# Revit family: TopVent_TH
name_source: partatom
category: Mechanical Equipment
revit_build: Autodesk Revit MEP 2015 (Build: 20160512_0715(x64)
units: mm (PartAtom-declared; Revit-internal decimal feet)

## types (6) — shared parameters
COBIE Extract air temperature max. = 50°C
COBIE Frequency = 50 Hz
COBIE Permitted voltage tolerance = +/-5%
COBIE Pressure of the heating medium max. = 800 kPa
COBIE Protection rating = IP 54
COBIE Series fuse = 13A
COBIE Supply air temperature max. = 60°C
COBIE Supply voltage = 3x400 V AC
COBIE Temperature of the heating medium max. = 90°C
Extract air temperature max. = 50°C
Frequency = 50 Hz
Permitted voltage tolerance = +/-5%
Pressure of the heating medium max. = 800 kPa
Protection rating = IP 54
Series fuse = 13A
Supply air temperature max. = 60°C
Supply voltage = 3x400 V AC
Temperature of the heating medium max. = 90°C

## per-type parameters (varying)
- TH-6-A: A=900 mm  [stored 2.95276 ft]; B=905 mm  [stored 2.96916 ft]; C=415 mm  [stored 1.36155 ft]; COBIE Connected load=1.5 kW; COBIE Current consumption max.=2.9A; COBIE Effective electric power input=0.46 kW; COBIE Floor area covered=537.0; COBIE Heat output 16/20 °C (60/40 °C)=18.8/16.2 kW; COBIE Heat output 16/20 °C (80/60 °C)=32.8/30.3 kW; COBIE Maximum mounting height 16/20 °C (60/40 °C)=16.8/17.9 m; COBIE Maximum mounting height 16/20 °C (80/60 °C)=13.4/14.0 m; COBIE Nominal air flow rate=6000.0; COBIE Octave sound power level - 1000 Hz=74 dB; COBIE Octave sound power level - 125 Hz=60 dB; COBIE Octave sound power level - 2000 Hz=70 dB; COBIE Octave sound power level - 250 Hz=65 dB; COBIE Octave sound power level - 4000 Hz=64 dB; COBIE Octave sound power level - 500 Hz=70 dB; COBIE Octave sound power level - 63 Hz=55 dB; COBIE Octave sound power level - 8000 Hz=56 dB; COBIE Sound pressure level (at a distance of 5 m)=55 dB(A); COBIE Static efficiency of the fans=48.5%; COBIE Supply air temperature 16/20 °C (60/40 °C)=27.3/30.0 °C; COBIE Supply air temperature 16/20 °C (80/60 °C)=34.2/37.0 °C; COBIE Total sound power level=77 dB(A); COBIE Water content of heating coil=4.6 l; COBIE Water pressure drop 16/20 °C (60/40 °C)=2/2 kPa; COBIE Water pressure drop 16/20 °C (80/60 °C)=7/6 kPa; COBIE Water quantity 16/20 °C (60/40 °C)=807/697 l/h; COBIE Water quantity 16/20 °C (80/60 °C)=1410/1301 l/h; COBIE Weight=104 kg; Connected load=1.5 kW; Current consumption max.=2.9A; E=594 mm  [stored 1.94882 ft]; E/2=297 mm  [stored 0.974409 ft]; Effective electric power input=0.46 kW; F=758 mm  [stored 2.48688 ft]; Floor area covered=537 m²; G=322 mm  [stored 1.05643 ft]; H=244 mm  [stored 0.800525 ft]; Heat output 16/20 °C (60/40 °C)=18.8/16.2 kW; Heat output 16/20 °C (80/60 °C)=32.8/30.3 kW; I=760 mm  [stored 2.49344 ft]; J=32 mm; K=1030 mm  [stored 3.37927 ft]; Maximum mounting height 16/20 °C (60/40 °C)=16.8/17.9 m; Maximum mounting height 16/20 °C (80/60 °C)=13.4/14.0 m; Nominal air flow rate=6000 m³/h; Octave sound power level - 1000 Hz=74 dB; Octave sound power level - 125 Hz=60 dB; Octave sound power level - 2000 Hz=70 dB; Octave sound power level - 250 Hz=65 dB; Octave sound power level - 4000 Hz=64 dB; Octave sound power level - 500 Hz=70 dB; Octave sound power level - 63 Hz=55 dB; Octave sound power level - 8000 Hz=56 dB; R=977 mm  [stored 3.20538 ft]; Sound pressure level (at a distance of 5 m)=55 dB(A); Static efficiency of the fans=48.5%; Supply air temperature 16/20 °C (60/40 °C)=27.3/30.0 °C; Supply air temperature 16/20 °C (80/60 °C)=34.2/37.0 °C; Total sound power level=77 dB(A); Water content of heating coil=4.6 l; Water pressure drop 16/20 °C (60/40 °C)=2/2 kPa; Water pressure drop 16/20 °C (80/60 °C)=7/6 kPa; Water quantity 16/20 °C (60/40 °C)=807/697 l/h; Water quantity 16/20 °C (80/60 °C)=1410/1301 l/h; Weight=104 kg
- TH-6-B: A=900 mm  [stored 2.95276 ft]; B=905 mm  [stored 2.96916 ft]; C=415 mm  [stored 1.36155 ft]; COBIE Connected load=1.5 kW; COBIE Current consumption max.=2.9A; COBIE Effective electric power input=0.53 kW; COBIE Floor area covered=537.0; COBIE Heat output 16/20 °C (60/40 °C)=26.9/23.3 kW; COBIE Heat output 16/20 °C (80/60 °C)=47.0/43.4 kW; COBIE Maximum mounting height 16/20 °C (60/40 °C)=14.6/15.5 m; COBIE Maximum mounting height 16/20 °C (80/60 °C)=11.6/12.0 m; COBIE Nominal air flow rate=6000.0; COBIE Octave sound power level - 1000 Hz=74 dB; COBIE Octave sound power level - 125 Hz=60 dB; COBIE Octave sound power level - 2000 Hz=70 dB; COBIE Octave sound power level - 250 Hz=65 dB; COBIE Octave sound power level - 4000 Hz=64 dB; COBIE Octave sound power level - 500 Hz=70 dB; COBIE Octave sound power level - 63 Hz=55 dB; COBIE Octave sound power level - 8000 Hz=56 dB; COBIE Sound pressure level (at a distance of 5 m)=55 dB(A); COBIE Static efficiency of the fans=48.5%; COBIE Supply air temperature 16/20 °C (60/40 °C)=31.1/33.5 °C; COBIE Supply air temperature 16/20 °C (80/60 °C)=41.3/43.5 °C; COBIE Total sound power level=77 dB(A); COBIE Water content of heating coil=4.6 l; COBIE Water pressure drop 16/20 °C (60/40 °C)=4/3 kPa; COBIE Water pressure drop 16/20 °C (80/60 °C)=13/11 kPa; COBIE Water quantity 16/20 °C (60/40 °C)=1157/1001 l/h; COBIE Water quantity 16/20 °C (80/60 °C)=2020/1864 l/h; COBIE Weight=104 kg; Connected load=1.5 kW; Current consumption max.=2.9A; E=594 mm  [stored 1.94882 ft]; E/2=297 mm  [stored 0.974409 ft]; Effective electric power input=0.53 kW; F=758 mm  [stored 2.48688 ft]; Floor area covered=537 m²; G=322 mm  [stored 1.05643 ft]; H=244 mm  [stored 0.800525 ft]; Heat output 16/20 °C (60/40 °C)=26.9/23.3 kW; Heat output 16/20 °C (80/60 °C)=47.0/43.4 kW; I=760 mm  [stored 2.49344 ft]; J=32 mm; K=1030 mm  [stored 3.37927 ft]; Maximum mounting height 16/20 °C (60/40 °C)=14.6/15.5 m; Maximum mounting height 16/20 °C (80/60 °C)=11.6/12.0 m; Nominal air flow rate=6000 m³/h; Octave sound power level - 1000 Hz=74 dB; Octave sound power level - 125 Hz=60 dB; Octave sound power level - 2000 Hz=70 dB; Octave sound power level - 250 Hz=65 dB; Octave sound power level - 4000 Hz=64 dB; Octave sound power level - 500 Hz=70 dB; Octave sound power level - 63 Hz=55 dB; Octave sound power level - 8000 Hz=56 dB; R=977 mm  [stored 3.20538 ft]; Sound pressure level (at a distance of 5 m)=55 dB(A); Static efficiency of the fans=48.5%; Supply air temperature 16/20 °C (60/40 °C)=31.1/33.5 °C; Supply air temperature 16/20 °C (80/60 °C)=41.3/43.5 °C; Total sound power level=77 dB(A); Water content of heating coil=4.6 l; Water pressure drop 16/20 °C (60/40 °C)=4/3 kPa; Water pressure drop 16/20 °C (80/60 °C)=13/11 kPa; Water quantity 16/20 °C (60/40 °C)=1157/1001 l/h; Water quantity 16/20 °C (80/60 °C)=2020/1864 l/h; Weight=104 kg
- TH-6-C: A=900 mm  [stored 2.95276 ft]; B=905 mm  [stored 2.96916 ft]; C=415 mm  [stored 1.36155 ft]; COBIE Connected load=1.5 kW; COBIE Current consumption max.=2.9A; COBIE Effective electric power input=0.74 kW; COBIE Floor area covered=537.0; COBIE Heat output 16/20 °C (60/40 °C)=45.0/39.3 kW; COBIE Heat output 16/20 °C (80/60 °C)=76.0/70.3 kW; COBIE Maximum mounting height 16/20 °C (60/40 °C)=11.8/12.5 m; COBIE Maximum mounting height 16/20 °C (80/60 °C)=9.4/9.8 m; COBIE Nominal air flow rate=6000.0; COBIE Octave sound power level - 1000 Hz=74 dB; COBIE Octave sound power level - 125 Hz=60 dB; COBIE Octave sound power level - 2000 Hz=70 dB; COBIE Octave sound power level - 250 Hz=65 dB; COBIE Octave sound power level - 4000 Hz=64 dB; COBIE Octave sound power level - 500 Hz=70 dB; COBIE Octave sound power level - 63 Hz=55 dB; COBIE Octave sound power level - 8000 Hz=56 dB; COBIE Sound pressure level (at a distance of 5 m)=55 dB(A); COBIE Static efficiency of the fans=48.5%; COBIE Supply air temperature 16/20 °C (60/40 °C)=40.3/41.5 °C; COBIE Supply air temperature 16/20 °C (80/60 °C)=55.6/56.8 °C; COBIE Total sound power level=77 dB(A); COBIE Water content of heating coil=7.9 l; COBIE Water pressure drop 16/20 °C (60/40 °C)=6/5 kPa; COBIE Water pressure drop 16/20 °C (80/60 °C)=18/16 kPa; COBIE Water quantity 16/20 °C (60/40 °C)=1935/1690 l/h; COBIE Water quantity 16/20 °C (80/60 °C)=3267/3022 l/h; COBIE Weight=111 kg; Connected load=1.5 kW; Current consumption max.=2.9A; E=594 mm  [stored 1.94882 ft]; E/2=297 mm  [stored 0.974409 ft]; Effective electric power input=0.74 kW; F=758 mm  [stored 2.48688 ft]; Floor area covered=537 m²; G=322 mm  [stored 1.05643 ft]; H=244 mm  [stored 0.800525 ft]; Heat output 16/20 °C (60/40 °C)=45.0/39.3 kW; Heat output 16/20 °C (80/60 °C)=76.0/70.3 kW; I=760 mm  [stored 2.49344 ft]; J=32 mm; K=1030 mm  [stored 3.37927 ft]; Maximum mounting height 16/20 °C (60/40 °C)=11.8/12.5 m; Maximum mounting height 16/20 °C (80/60 °C)=9.4/9.8 m; Nominal air flow rate=6000 m³/h; Octave sound power level - 1000 Hz=74 dB; Octave sound power level - 125 Hz=60 dB; Octave sound power level - 2000 Hz=70 dB; Octave sound power level - 250 Hz=65 dB; Octave sound power level - 4000 Hz=64 dB; Octave sound power level - 500 Hz=70 dB; Octave sound power level - 63 Hz=55 dB; Octave sound power level - 8000 Hz=56 dB; R=977 mm  [stored 3.20538 ft]; Sound pressure level (at a distance of 5 m)=55 dB(A); Static efficiency of the fans=48.5%; Supply air temperature 16/20 °C (60/40 °C)=40.3/41.5 °C; Supply air temperature 16/20 °C (80/60 °C)=55.6/56.8 °C; Total sound power level=77 dB(A); Water content of heating coil=7.9 l; Water pressure drop 16/20 °C (60/40 °C)=6/5 kPa; Water pressure drop 16/20 °C (80/60 °C)=18/16 kPa; Water quantity 16/20 °C (60/40 °C)=1935/1690 l/h; Water quantity 16/20 °C (80/60 °C)=3267/3022 l/h; Weight=111 kg
- TH-9-A: A=1100 mm; B=1050 mm; C=480 mm  [stored 1.5748 ft]; COBIE Connected load=2.1 kW; COBIE Current consumption max.=4.0A; COBIE Effective electric power input=0.84 kW; COBIE Floor area covered=946.0; COBIE Heat output 16/20 °C (60/40 °C)=31.7/27.4 kW; COBIE Heat output 16/20 °C (80/60 °C)=55.5/51.2 kW; COBIE Maximum mounting height 16/20 °C (60/40 °C)=17.0/18.1 m; COBIE Maximum mounting height 16/20 °C (80/60 °C)=13.6/14.1 m; COBIE Nominal air flow rate=9000.0; COBIE Octave sound power level - 1000 Hz=75 dB; COBIE Octave sound power level - 125 Hz=65 dB; COBIE Octave sound power level - 2000 Hz=75 dB; COBIE Octave sound power level - 250 Hz=69 dB; COBIE Octave sound power level - 4000 Hz=70 dB; COBIE Octave sound power level - 500 Hz=73 dB; COBIE Octave sound power level - 63 Hz=61 dB; COBIE Octave sound power level - 8000 Hz=63 dB; COBIE Sound pressure level (at a distance of 5 m)=58 dB(A); COBIE Static efficiency of the fans=43.0%; COBIE Supply air temperature 16/20 °C (60/40 °C)=28.5/31.1 °C; COBIE Supply air temperature 16/20 °C (80/60 °C)=36.6/38.9 °C; COBIE Total sound power level=80 dB(A); COBIE Water content of heating coil=7.4 l; COBIE Water pressure drop 16/20 °C (60/40 °C)=3/2 kPa; COBIE Water pressure drop 16/20 °C (80/60 °C)=8/7 kPa; COBIE Water quantity 16/20 °C (60/40 °C)=1364/1179 l/h; COBIE Water quantity 16/20 °C (80/60 °C)=2386/2201 l/h; COBIE Weight=155 kg; Connected load=2.1 kW; Current consumption max.=4.0A; E=846 mm  [stored 2.77559 ft]; E/2=423 mm  [stored 1.3878 ft]; Effective electric power input=0.84 kW; F=882 mm  [stored 2.8937 ft]; Floor area covered=946 m²; G=367 mm  [stored 1.20407 ft]; H=289 mm  [stored 0.948163 ft]; Heat output 16/20 °C (60/40 °C)=31.7/27.4 kW; Heat output 16/20 °C (80/60 °C)=55.5/51.2 kW; I=935 mm; J=38 mm; K=1230 mm  [stored 4.03543 ft]; Maximum mounting height 16/20 °C (60/40 °C)=17.0/18.1 m; Maximum mounting height 16/20 °C (80/60 °C)=13.6/14.1 m; Nominal air flow rate=9000 m³/h; Octave sound power level - 1000 Hz=75 dB; Octave sound power level - 125 Hz=65 dB; Octave sound power level - 2000 Hz=75 dB; Octave sound power level - 250 Hz=69 dB; Octave sound power level - 4000 Hz=70 dB; Octave sound power level - 500 Hz=73 dB; Octave sound power level - 63 Hz=61 dB; Octave sound power level - 8000 Hz=63 dB; R=1152 mm  [stored 3.77953 ft]; Sound pressure level (at a distance of 5 m)=58 dB(A); Static efficiency of the fans=43.0%; Supply air temperature 16/20 °C (60/40 °C)=28.5/31.1 °C; Supply air temperature 16/20 °C (80/60 °C)=36.6/38.9 °C; Total sound power level=80 dB(A); Water content of heating coil=7.4 l; Water pressure drop 16/20 °C (60/40 °C)=3/2 kPa; Water pressure drop 16/20 °C (80/60 °C)=8/7 kPa; Water quantity 16/20 °C (60/40 °C)=1364/1179 l/h; Water quantity 16/20 °C (80/60 °C)=2386/2201 l/h; Weight=155 kg
- TH-9-B: A=1100 mm; B=1050 mm; C=480 mm  [stored 1.5748 ft]; COBIE Connected load=2.1 kW; COBIE Current consumption max.=4.0A; COBIE Effective electric power input=0.96 kW; COBIE Floor area covered=946.0; COBIE Heat output 16/20 °C (60/40 °C)=40.6/35.1 kW; COBIE Heat output 16/20 °C (80/60 °C)=71.2/65.7 kW; COBIE Maximum mounting height 16/20 °C (60/40 °C)=15.4/16.5 m; COBIE Maximum mounting height 16/20 °C (80/60 °C)=12.2/12.7 m; COBIE Nominal air flow rate=9000.0; COBIE Octave sound power level - 1000 Hz=75 dB; COBIE Octave sound power level - 125 Hz=65 dB; COBIE Octave sound power level - 2000 Hz=75 dB; COBIE Octave sound power level - 250 Hz=69 dB; COBIE Octave sound power level - 4000 Hz=70 dB; COBIE Octave sound power level - 500 Hz=73 dB; COBIE Octave sound power level - 63 Hz=61 dB; COBIE Octave sound power level - 8000 Hz=63 dB; COBIE Sound pressure level (at a distance of 5 m)=58 dB(A); COBIE Static efficiency of the fans=43.0%; COBIE Supply air temperature 16/20 °C (60/40 °C)=31.4/33.6 °C; COBIE Supply air temperature 16/20 °C (80/60 °C)=41.5/43.7 °C; COBIE Total sound power level=80 dB(A); COBIE Water content of heating coil=7.4 l; COBIE Water pressure drop 16/20 °C (60/40 °C)=4/3 kPa; COBIE Water pressure drop 16/20 °C (80/60 °C)=12/10 kPa; COBIE Water quantity 16/20 °C (60/40 °C)=1746/1509 l/h; COBIE Water quantity 16/20 °C (80/60 °C)=3060/2823 l/h; COBIE Weight=155 kg; Connected load=2.1 kW; Current consumption max.=4.0A; E=846 mm  [stored 2.77559 ft]; E/2=423 mm  [stored 1.3878 ft]; Effective electric power input=0.96 kW; F=882 mm  [stored 2.8937 ft]; Floor area covered=946 m²; G=367 mm  [stored 1.20407 ft]; H=289 mm  [stored 0.948163 ft]; Heat output 16/20 °C (60/40 °C)=40.6/35.1 kW; Heat output 16/20 °C (80/60 °C)=71.2/65.7 kW; I=935 mm; J=38 mm; K=1230 mm  [stored 4.03543 ft]; Maximum mounting height 16/20 °C (60/40 °C)=15.4/16.5 m; Maximum mounting height 16/20 °C (80/60 °C)=12.2/12.7 m; Nominal air flow rate=9000 m³/h; Octave sound power level - 1000 Hz=75 dB; Octave sound power level - 125 Hz=65 dB; Octave sound power level - 2000 Hz=75 dB; Octave sound power level - 250 Hz=69 dB; Octave sound power level - 4000 Hz=70 dB; Octave sound power level - 500 Hz=73 dB; Octave sound power level - 63 Hz=61 dB; Octave sound power level - 8000 Hz=63 dB; R=1152 mm  [stored 3.77953 ft]; Sound pressure level (at a distance of 5 m)=58 dB(A); Static efficiency of the fans=43.0%; Supply air temperature 16/20 °C (60/40 °C)=31.4/33.6 °C; Supply air temperature 16/20 °C (80/60 °C)=41.5/43.7 °C; Total sound power level=80 dB(A); Water content of heating coil=7.4 l; Water pressure drop 16/20 °C (60/40 °C)=4/3 kPa; Water pressure drop 16/20 °C (80/60 °C)=12/10 kPa; Water quantity 16/20 °C (60/40 °C)=1746/1509 l/h; Water quantity 16/20 °C (80/60 °C)=3060/2823 l/h; Weight=155 kg
- TH-9-C: A=1100 mm; B=1050 mm; C=480 mm  [stored 1.5748 ft]; COBIE Connected load=2.1 kW; COBIE Current consumption max.=4.0A; COBIE Effective electric power input=1.26 kW; COBIE Floor area covered=946.0; COBIE Heat output 16/20 °C (60/40 °C)=69.9/61.1 kW; COBIE Heat output 16/20 °C (80/60 °C)=117.9/109.1 kW; COBIE Maximum mounting height 16/20 °C (60/40 °C)=12.3/13.1 m; COBIE Maximum mounting height 16/20 °C (80/60 °C)=9.8/10.2 m; COBIE Nominal air flow rate=9000.0; COBIE Octave sound power level - 1000 Hz=75 dB; COBIE Octave sound power level - 125 Hz=65 dB; COBIE Octave sound power level - 2000 Hz=75 dB; COBIE Octave sound power level - 250 Hz=69 dB; COBIE Octave sound power level - 4000 Hz=70 dB; COBIE Octave sound power level - 500 Hz=73 dB; COBIE Octave sound power level - 63 Hz=61 dB; COBIE Octave sound power level - 8000 Hz=63 dB; COBIE Sound pressure level (at a distance of 5 m)=58 dB(A); COBIE Static efficiency of the fans=43.0%; COBIE Supply air temperature 16/20 °C (60/40 °C)=41.1/42.1 °C; COBIE Supply air temperature 16/20 °C (80/60 °C)=56.9/58.0 °C; COBIE Total sound power level=80 dB(A); COBIE Water content of heating coil=12.4 l; COBIE Water pressure drop 16/20 °C (60/40 °C)=6/5 kPa; COBIE Water pressure drop 16/20 °C (80/60 °C)=18/15 kPa; COBIE Water quantity 16/20 °C (60/40 °C)=3003/2622 l/h; COBIE Water quantity 16/20 °C (80/60 °C)=5066/4686 l/h; COBIE Weight=166 kg; Connected load=2.1 kW; Current consumption max.=4.0A; E=846 mm  [stored 2.77559 ft]; E/2=423 mm  [stored 1.3878 ft]; Effective electric power input=1.26 kW; F=882 mm  [stored 2.8937 ft]; Floor area covered=946 m²; G=367 mm  [stored 1.20407 ft]; H=289 mm  [stored 0.948163 ft]; Heat output 16/20 °C (60/40 °C)=69.9/61.1 kW; Heat output 16/20 °C (80/60 °C)=117.9/109.1 kW; I=935 mm; J=38 mm; K=1230 mm  [stored 4.03543 ft]; Maximum mounting height 16/20 °C (60/40 °C)=12.3/13.1 m; Maximum mounting height 16/20 °C (80/60 °C)=9.8/10.2 m; Nominal air flow rate=9000 m³/h; Octave sound power level - 1000 Hz=75 dB; Octave sound power level - 125 Hz=65 dB; Octave sound power level - 2000 Hz=75 dB; Octave sound power level - 250 Hz=69 dB; Octave sound power level - 4000 Hz=70 dB; Octave sound power level - 500 Hz=73 dB; Octave sound power level - 63 Hz=61 dB; Octave sound power level - 8000 Hz=63 dB; R=1152 mm  [stored 3.77953 ft]; Sound pressure level (at a distance of 5 m)=58 dB(A); Static efficiency of the fans=43.0%; Supply air temperature 16/20 °C (60/40 °C)=41.1/42.1 °C; Supply air temperature 16/20 °C (80/60 °C)=56.9/58.0 °C; Total sound power level=80 dB(A); Water content of heating coil=12.4 l; Water pressure drop 16/20 °C (60/40 °C)=6/5 kPa; Water pressure drop 16/20 °C (80/60 °C)=18/15 kPa; Water quantity 16/20 °C (60/40 °C)=3003/2622 l/h; Water quantity 16/20 °C (80/60 °C)=5066/4686 l/h; Weight=166 kg

note: [stored X ft] marks values corroborated as IEEE doubles in the binary element streams (Revit-internal decimal feet)

## geometry (parser evidence)
native form markers: Sweep x7
no freeform markers — native parametric forms only
